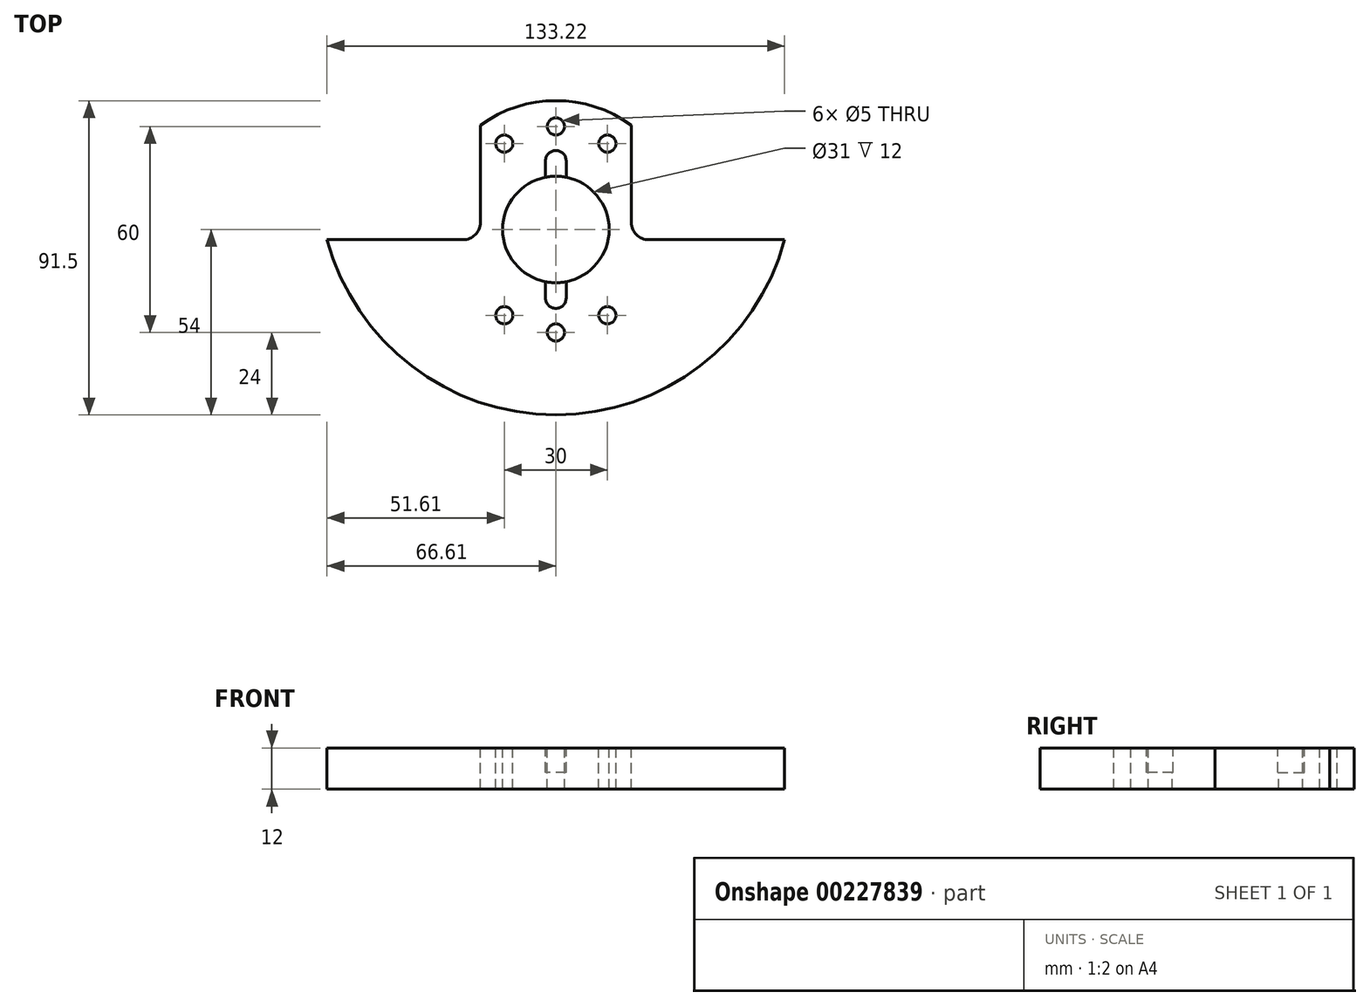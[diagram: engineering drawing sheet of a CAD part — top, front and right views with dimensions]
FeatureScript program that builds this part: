
annotation { "Feature Type Name" : "Feature", "Feature Type Description" : "" }
export const myFeature = defineFeature(function(context is Context, id is Id, definition is map)
    precondition{}
    {
        {
            var Q0;
            Q0=qCreatedBy(makeId("Top.planeOp"),FACE);
            var sketch = newSketch(context, id + "F0", { "sketchPlane" : qUnion([Q0])});
            skArc(sketch, "E0", {"start": v(-15.2, -3) * mm, "mid": v(0, -15.5) * mm, "end": v(15.2, -3) * mm});
            skArc(sketch, "E1", {"start": v(-66.61, -3) * mm, "mid": v(0, -54) * mm, "end": v(66.61, -3) * mm});
            skLineSegment(sketch, "E2", {"start": v(-66.61, -3) * mm, "end": v(-15.2, -3) * mm});
            skLineSegment(sketch, "E3.trimOffspring", {"start": v(15.2, -3) * mm, "end": v(66.61, -3) * mm});
            skCircle(sketch, "E4", {"center": v(-16, -15) * mm, "radius": 2.5 * mm, "construction": true});
            skCircle(sketch, "E5", {"center": v(0, -30) * mm, "radius": 2.5 * mm});
            skCircle(sketch, "E6", {"center": v(0, 15) * mm, "radius": 55 * mm, "construction": true});
            skCircle(sketch, "E7", {"center": v(-16, -25) * mm, "radius": 2.5 * mm});
            skCircle(sketch, "E8.MirrorC", {"center": v(16, -15) * mm, "radius": 2.5 * mm, "construction": true});
            skCircle(sketch, "E9.MirrorC", {"center": v(16, -25) * mm, "radius": 2.5 * mm});
            skCircle(sketch, "E10", {"center": v(0, 15) * mm, "radius": 50 * mm, "construction": true});
            skLineSegment(sketch, "E11.MirrorCS", {"start": v(0, 15) * mm, "end": v(78.85, -30.52) * mm, "construction": true});
            skCircle(sketch, "E12", {"center": v(43.3, -10) * mm, "radius": 20 * mm, "construction": true});
            skSolve(sketch);
        }
        {
            var Q0;
            Q0=qCreatedBy(makeId("Top.planeOp"),FACE);
            cPlane(context, id + "F1", {"entities" : qUnion([Q0]), "cplaneType" : CPlaneType.OFFSET, "offset" : 19 * mm, "oppositeDirection" : true, "width" : 150 * mm, "height" : 150 * mm});
        }
        {
            var Q0;
            Q0=qCreatedBy(id+"F1.planeOp",FACE);
            var sketch = newSketch(context, id + "F2", { "sketchPlane" : qUnion([Q0])});
            skLineSegment(sketch, "E13.0.0", {"start": v(-27, -3) * mm, "end": v(-66.61, -3) * mm});
            skArc(sketch, "E13.0.1", {"start": v(-66.61, -3) * mm, "mid": v(0, -54) * mm, "end": v(66.61, -3) * mm});
            skLineSegment(sketch, "E13.0.2", {"start": v(66.61, -3) * mm, "end": v(27, -3) * mm});
            skCircle(sketch, "E14.0", {"center": v(-16, -15) * mm, "radius": 2.5 * mm, "construction": true});
            skCircle(sketch, "E14.1", {"center": v(16, -15) * mm, "radius": 2.5 * mm, "construction": true});
            skCircle(sketch, "E14.2", {"center": v(-15, -25) * mm, "radius": 2.5 * mm});
            skCircle(sketch, "E14.3", {"center": v(0, -30) * mm, "radius": 2.5 * mm});
            skLineSegment(sketch, "E15", {"start": v(-22, 30.37) * mm, "end": v(-22, 2) * mm});
            skCircle(sketch, "E16", {"center": v(0, 0) * mm, "radius": 15.5 * mm});
            skLineSegment(sketch, "E17.MirrorCS", {"start": v(22, 30.37) * mm, "end": v(22, 2) * mm});
            skArc(sketch, "E18.trimOffspring", {"start": v(22, 30.37) * mm, "mid": v(0, 37.5) * mm, "end": v(-22, 30.37) * mm});
            skCircle(sketch, "E19.MirrorC", {"center": v(15, -25) * mm, "radius": 2.5 * mm});
            skCircle(sketch, "E20.MirrorC", {"center": v(-15, 25) * mm, "radius": 2.5 * mm});
            skCircle(sketch, "E21.MirrorC", {"center": v(15, 25) * mm, "radius": 2.5 * mm});
            skCircle(sketch, "E22.MirrorC", {"center": v(0, 30) * mm, "radius": 2.5 * mm});
            skPoint(sketch, "E23.visualSharp", {"position": v(-22, -3) * mm});
            skArc(sketch, "E23.filletArc", {"start": v(-27, -3) * mm, "mid": v(-23.46, -1.54) * mm, "end": v(-22, 2) * mm});
            skPoint(sketch, "E24.visualSharp", {"position": v(22, -3) * mm});
            skArc(sketch, "E24.filletArc", {"start": v(22, 2) * mm, "mid": v(23.46, -1.54) * mm, "end": v(27, -3) * mm});
            skSolve(sketch);
        }
        {
            var Q0;
            Q0 = qSketchRegion(id + "F2", true);
            extrude(context, id + "F3", {"entities" : qUnion([Q0]), "oppositeDirection" : true, "depth" : 12 * mm});
        }
        {
            var Q0;
            Q0=qCreatedBy(id+"F1.planeOp",FACE);
            var sketch = newSketch(context, id + "F4", { "sketchPlane" : qUnion([Q0])});
            skLineSegment(sketch, "E25", {"start": v(-3, 20) * mm, "end": v(-3, 0) * mm});
            skLineSegment(sketch, "E26.MirrorCS", {"start": v(3, 20) * mm, "end": v(3, 0) * mm});
            skArc(sketch, "E27", {"start": v(3, 20) * mm, "mid": v(0, 23) * mm, "end": v(-3, 20) * mm});
            skArc(sketch, "E28.MirrorCS", {"start": v(3, -20) * mm, "mid": v(0, -23) * mm, "end": v(-3, -20) * mm});
            skLineSegment(sketch, "E29.MirrorCS", {"start": v(-3, -20) * mm, "end": v(-3, 0) * mm});
            skLineSegment(sketch, "E30.MirrorCS", {"start": v(3, -20) * mm, "end": v(3, 0) * mm});
            skSolve(sketch);
        }
        {
            var Q0;
            Q0 = qSketchRegion(id + "F4", true);
            extrude(context, id + "F5", {"entities" : qUnion([Q0]), "operationType" : NewBodyOperationType.REMOVE, "oppositeDirection" : true, "depth" : 7.1 * mm});
        }
    });
